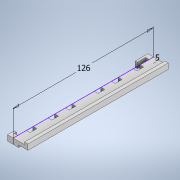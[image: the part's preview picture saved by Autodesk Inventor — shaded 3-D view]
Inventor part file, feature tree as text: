
AUTODESK INVENTOR PART (.ipt)
format: ipt  version: 2022 (Build 260153000, 153)  size: 186,368 bytes
history: native  units: in
note: dims shown in document units (in); Inventor stores cm internally (conversion verified against a paired STEP export)
features: extrude x5, sketch x5
ambient origin geometry x8: Origin, YZ Plane, XZ Plane, XY Plane, X Axis, Y Axis, Z Axis, Center Point
bodies: Solid1 (feature_tree)
feature tree (10):
  extrude  "Extrusion1"  Depth=0.1969in
  extrude  "Extrusion2"  Depth=0.1575in
  extrude  "Extrusion3"  Depth=0.1969in TaperAngle=0.0deg
  extrude  "Extrusion4"  Depth=0.0787in
  extrude  "Extrusion5"  Depth=0.1181in
  sketch  "Sketch1"  dims[d0=4.9606in d1=0.1969in]
  sketch  "Sketch2"  dims[d2=0.1969in d3=0.0in d4=0.1575in]
  sketch  "Sketch3"  dims[d5=0.1575in d6=0.1969in d7=0.0in]
  sketch  "Sketch4"  dims[d8=0.0787in d9=0.0787in]
  sketch  "Sketch5"  dims[d10=0.1969in d11=0.0in d12=0.1181in d13=0.1181in d14=0.0787in d15=0.1969in d16=0.0in d17=0.0in d18=0.2362in d20=0.2362in d21=1.0039in d22=1.0039in d25=0.2362in d26=0.2362in d27=1.7717in d28=1.7717in d29=0.3937in d30=0.0in d31=0.1378in d32=0.1378in d33=0.2362in d34=0.2362in d35=0.3937in d36=0.3937in]
